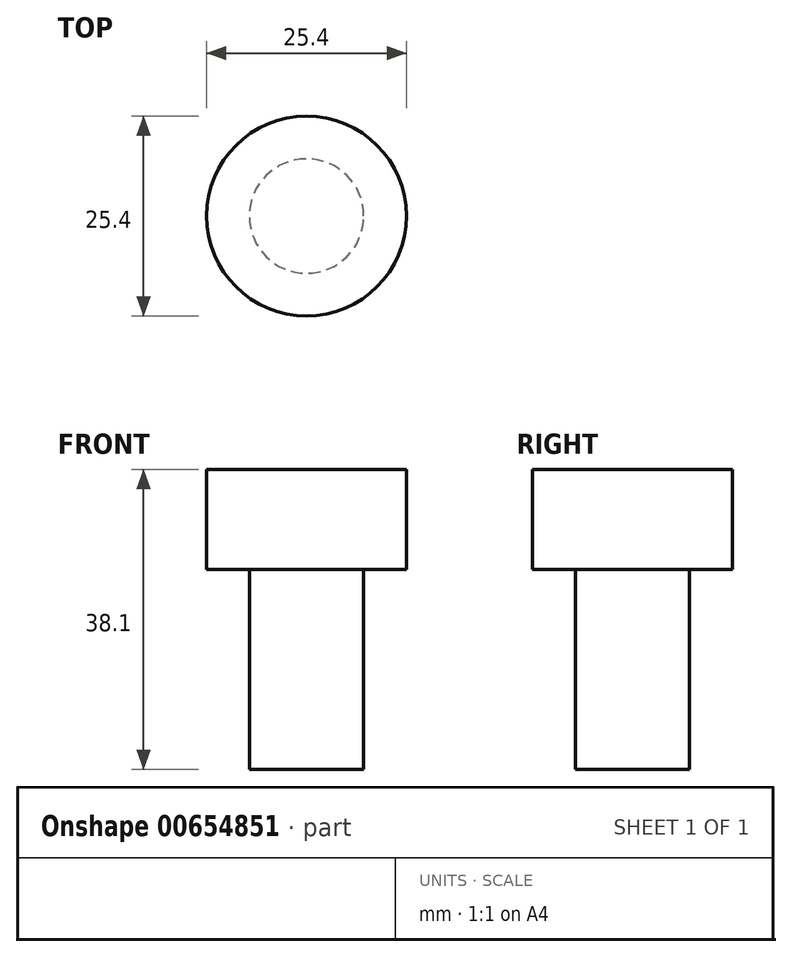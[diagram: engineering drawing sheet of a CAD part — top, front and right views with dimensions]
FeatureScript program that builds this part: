
annotation { "Feature Type Name" : "Feature", "Feature Type Description" : "" }
export const myFeature = defineFeature(function(context is Context, id is Id, definition is map)
    precondition{}
    {
        {
            var Q0;
            Q0=qCreatedBy(makeId("Top.planeOp"),FACE);
            var sketch = newSketch(context, id + "F0", { "sketchPlane" : qUnion([Q0])});
            skCircle(sketch, "E0", {"center": v(0, 0) * mm, "radius": 12.7 * mm});
            skSolve(sketch);
        }
        {
            var Q0;
            Q0=makeQuery(id+"F0.imprint","IMPRINT",FACE,{"disambiguationData":[TD([[makeQuery(id+"F0.imprint","IMPRINT",EDGE,{"derivedFrom":sQuery(id+"F0.wireOp",EDGE,"E0")}),1.0]])]});
            extrude(context, id + "F1", {"entities" : qUnion([Q0]), "depth" : 12.7 * mm, "offsetDistance" : 25.4 * mm});
        }
        {
            var Q0;
            Q0=makeQuery(id+"F1.opExtrude","CAP_FACE",FACE,{"disambiguationData":[OSD([sQuery(id+"F0.wireOp",EDGE,"E0")])],"isStart":true});
            var sketch = newSketch(context, id + "F2", { "sketchPlane" : qUnion([Q0])});
            skCircle(sketch, "E1", {"center": v(0, 0) * mm, "radius": 7.26 * mm});
            skSolve(sketch);
        }
        {
            var Q0;
            Q0 = qSketchRegion(id + "F2", true);
            extrude(context, id + "F3", {"entities" : qUnion([Q0]), "operationType" : NewBodyOperationType.ADD, "depth" : 25.4 * mm, "offsetDistance" : 25.4 * mm});
        }
    });
